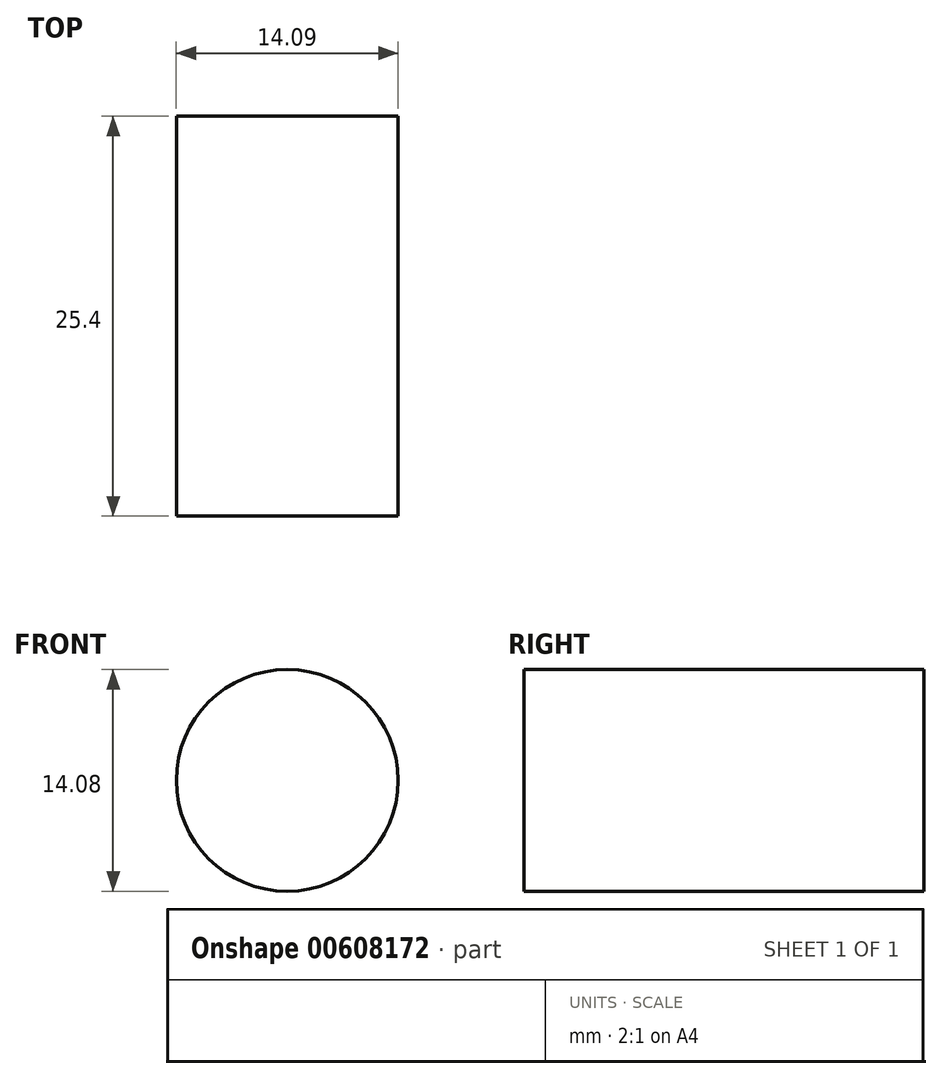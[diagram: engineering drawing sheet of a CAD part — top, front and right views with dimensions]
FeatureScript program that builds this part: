
annotation { "Feature Type Name" : "Feature", "Feature Type Description" : "" }
export const myFeature = defineFeature(function(context is Context, id is Id, definition is map)
    precondition{}
    {
        {
            var Q0;
            Q0=qCreatedBy(makeId("Front.planeOp"),FACE);
            var sketch = newSketch(context, id + "F0", { "sketchPlane" : qUnion([Q0])});
            skCircle(sketch, "E0", {"center": v(67.23, 0) * mm, "radius": 7.04 * mm});
            skSolve(sketch);
        }
        {
            var Q0;
            Q0 = qSketchRegion(id + "F0", true);
            extrude(context, id + "F1", {"entities" : qUnion([Q0]), "depth" : 25.4 * mm, "offsetDistance" : 25.4 * mm});
        }
    });
